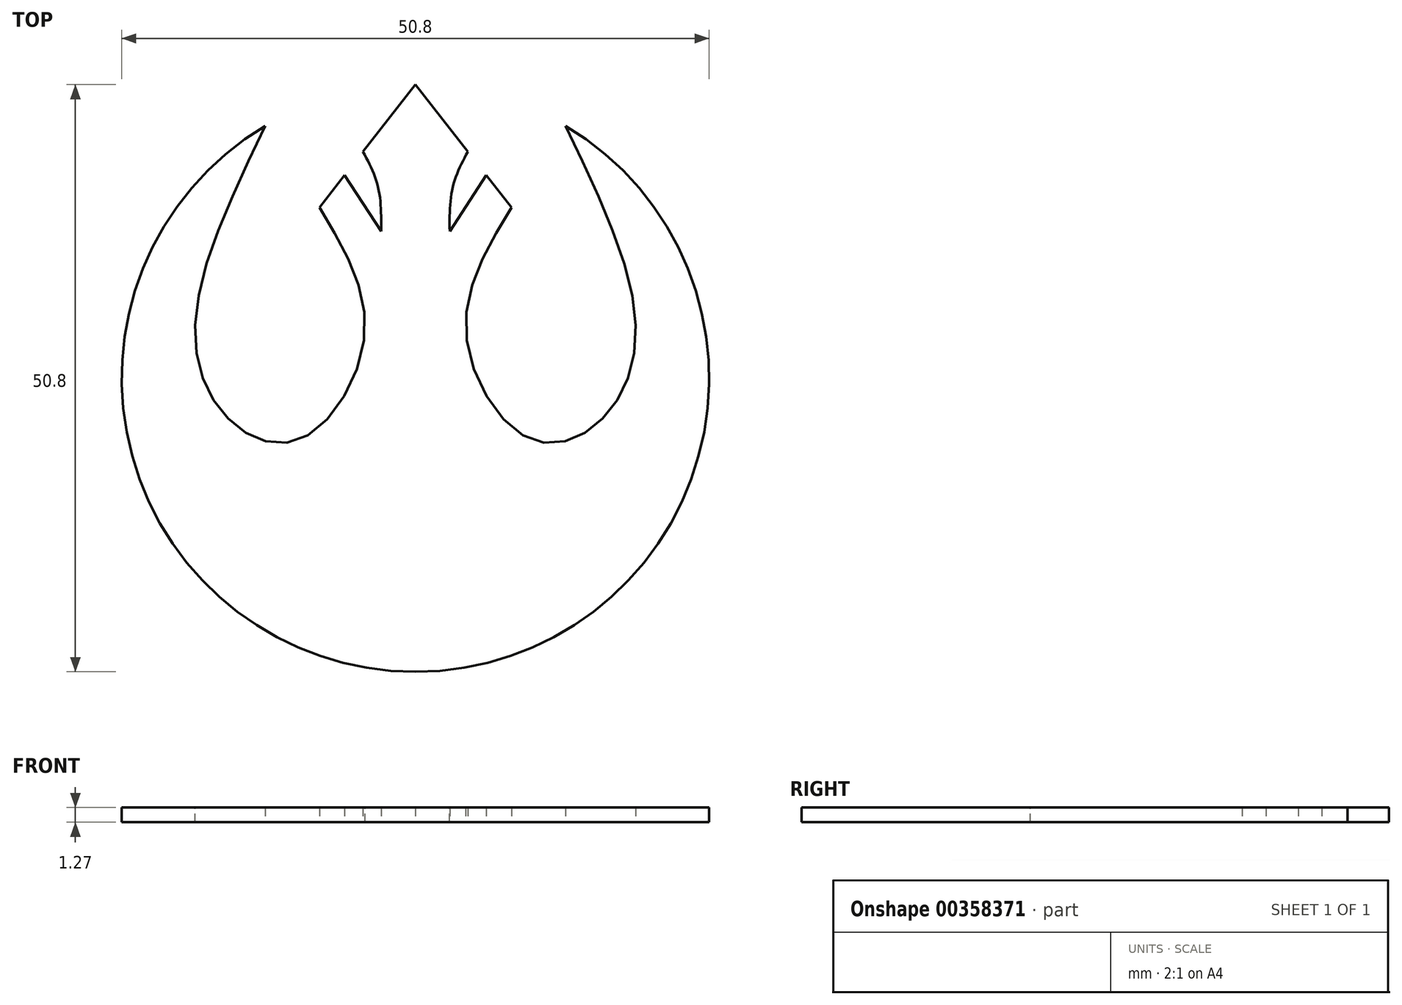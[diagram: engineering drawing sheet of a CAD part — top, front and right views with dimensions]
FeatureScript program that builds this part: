
annotation { "Feature Type Name" : "Feature", "Feature Type Description" : "" }
export const myFeature = defineFeature(function(context is Context, id is Id, definition is map)
    precondition{}
    {
        {
            var Q0;
            Q0=qCreatedBy(makeId("Top.planeOp"),FACE);
            var sketch = newSketch(context, id + "F0", { "sketchPlane" : qUnion([Q0])});
            skArc(sketch, "E0", {"start": v(-36.16, 53.46) * mm, "mid": v(-61.56, 28.06) * mm, "end": v(-36.16, 2.66) * mm});
            skLineSegment(sketch, "E1", {"start": v(-36.16, 53.46) * mm, "end": v(-36.16, 2.66) * mm});
            skLineSegment(sketch, "E2", {"start": v(-44.46, 42.82) * mm, "end": v(-36.16, 53.46) * mm});
            skLineSegment(sketch, "E3", {"start": v(-42.28, 45.62) * mm, "end": v(-39.13, 40.76) * mm});
            skFitSpline(sketch, "E4", {"points": [v(-40.69, 47.66) * mm, v(-39.38, 44.57) * mm, v(-39.13, 40.76) * mm], "startDerivative": vector(3.24, -6.13) * mm, "endDerivative": vector(-0.1, -7.65) * mm});
            skFitSpline(sketch, "E5", {"points": [v(-49.14, 49.89) * mm, v(-55.21, 32.66) * mm, v(-52.14, 24.37) * mm, v(-46.1, 22.8) * mm, v(-40.53, 31.92) * mm, v(-44.46, 42.82) * mm], "startDerivative": vector(-33.92, -70.48) * mm, "endDerivative": vector(-30.58, 50.45) * mm});
            skSolve(sketch);
        }
        {
            var Q0;
            {var subQ1=sQuery(id+"F0.wireOp",EDGE,"E1");Q0=makeQuery(id+"F0.imprint","IMPRINT",FACE,{"disambiguationData":[TD([[makeQuery(id+"F0.imprint","IMPRINT",EDGE,{"derivedFrom":subQ1}),-1.0]])]});}
            extrude(context, id + "F1", {"entities" : qUnion([Q0]), "depth" : 1.27 * mm});
        }
        {
            var Q0;
            Q0=makeQuery(id+"F1.opExtrude","SWEPT_BODY",BODY,{"disambiguationData":[OSD([sQuery(id+"F0.wireOp",EDGE,"E0"),sQuery(id+"F0.wireOp",EDGE,"E1"),sQuery(id+"F0.wireOp",EDGE,"E2"),sQuery(id+"F0.wireOp",EDGE,"E3"),sQuery(id+"F0.wireOp",EDGE,"E4"),sQuery(id+"F0.wireOp",EDGE,"E5")])]});
            var Q1;
            Q1=makeQuery(id+"F1.opExtrude","SWEPT_FACE",FACE,{"disambiguationData":[OSD([sQuery(id+"F0.wireOp",EDGE,"E1")])]});
            mirror(context, id + "F2", {"operationType" : NewBodyOperationType.ADD, "entities" : qUnion([Q0]), "mirrorPlane" : qUnion([Q1])});
        }
    });
